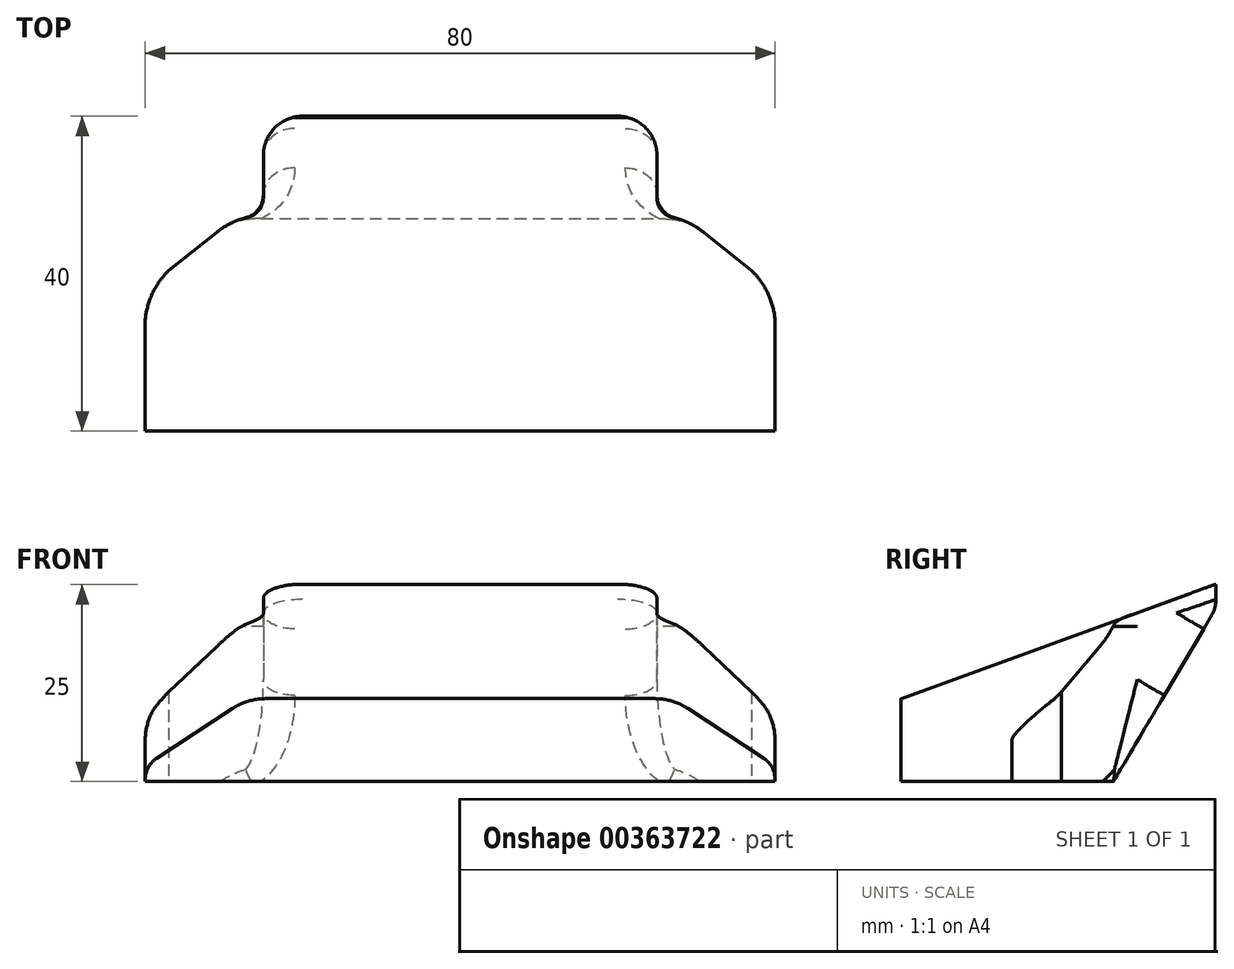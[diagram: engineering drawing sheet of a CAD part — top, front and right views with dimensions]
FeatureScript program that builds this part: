
annotation { "Feature Type Name" : "Feature", "Feature Type Description" : "" }
export const myFeature = defineFeature(function(context is Context, id is Id, definition is map)
    precondition{}
    {
        {
            var Q0;
            Q0=qCreatedBy(makeId("Top.planeOp"),FACE);
            var sketch = newSketch(context, id + "F0", { "sketchPlane" : qUnion([Q0])});
            skLineSegment(sketch, "E0", {"start": v(40, 0) * mm, "end": v(-40, 0) * mm});
            skLineSegment(sketch, "E1", {"start": v(-40, 0) * mm, "end": v(-40, 18) * mm});
            skLineSegment(sketch, "E2", {"start": v(-40, 18) * mm, "end": v(-28.75, 27) * mm});
            skLineSegment(sketch, "E3", {"start": v(-28.75, 27) * mm, "end": v(28.75, 27) * mm});
            skLineSegment(sketch, "E4", {"start": v(28.75, 27) * mm, "end": v(40, 18) * mm});
            skLineSegment(sketch, "E5", {"start": v(0, 40) * mm, "end": v(0, 0) * mm, "construction": true});
            skLineSegment(sketch, "E6", {"start": v(40, 18) * mm, "end": v(40, 0) * mm});
            skLineSegment(sketch, "E7", {"start": v(-25, 27) * mm, "end": v(-25, 40) * mm});
            skLineSegment(sketch, "E8", {"start": v(-25, 40) * mm, "end": v(25, 40) * mm});
            skLineSegment(sketch, "E9", {"start": v(25, 40) * mm, "end": v(25, 27) * mm});
            skSolve(sketch);
        }
        {
            var Q0;
            Q0 = qSketchRegion(id + "F0", true);
            extrude(context, id + "F1", {"entities" : qUnion([Q0]), "depth" : 25 * mm, "offsetDistance" : 25 * mm});
        }
        {
            var Q0;
            Q0=makeQuery(id+"F1.opExtrude","CAP_EDGE",EDGE,{"disambiguationData":[OSD([sQuery(id+"F0.wireOp",EDGE,"E0")])],"isStart":false});
            chamfer(context, id + "F2", {"entities" : qUnion([Q0]), "chamferType" : ChamferType.OFFSET_ANGLE, "width" : 14.5 * mm, "oppositeDirection" : false, "angle" : 70 * degree, "tangentPropagation" : true});
        }
        {
            var Q0;
            Q0=makeQuery(id+"F1.opExtrude","CAP_EDGE",EDGE,{"disambiguationData":[OSD([sQuery(id+"F0.wireOp",EDGE,"E8")])],"isStart":true});
            chamfer(context, id + "F3", {"entities" : qUnion([Q0]), "chamferType" : ChamferType.TWO_OFFSETS, "width1" : 13 * mm, "oppositeDirection" : false, "width2" : 22 * mm, "tangentPropagation" : true});
        }
        {
            var Q0;
            Q0=makeQuery(id+"F2.opChamfer","BLEND_EDGE",EDGE,{"blendedFrom":[makeQuery(id+"F1.opExtrude","CAP_EDGE",EDGE,{"disambiguationData":[OSD([sQuery(id+"F0.wireOp",EDGE,"E0")])],"isStart":false}),makeQuery(id+"F1.opExtrude","SWEPT_FACE",FACE,{"disambiguationData":[OSD([sQuery(id+"F0.wireOp",EDGE,"E1")])]})],"blendedInto":[makeQuery(id+"F1.opExtrude","SWEPT_FACE",FACE,{"disambiguationData":[OSD([sQuery(id+"F0.wireOp",EDGE,"E1")])]})]});
            var Q1;
            Q1=makeQuery(id+"F2.opChamfer","BLEND_EDGE",EDGE,{"blendedFrom":[makeQuery(id+"F1.opExtrude","CAP_EDGE",EDGE,{"disambiguationData":[OSD([sQuery(id+"F0.wireOp",EDGE,"E0")])],"isStart":false}),makeQuery(id+"F1.opExtrude","SWEPT_FACE",FACE,{"disambiguationData":[OSD([sQuery(id+"F0.wireOp",EDGE,"E6")])]})],"blendedInto":[makeQuery(id+"F1.opExtrude","SWEPT_FACE",FACE,{"disambiguationData":[OSD([sQuery(id+"F0.wireOp",EDGE,"E6")])]})]});
            chamfer(context, id + "F4", {"entities" : qUnion([Q0, Q1]), "chamferType" : ChamferType.TWO_OFFSETS, "width1" : 8 * mm, "oppositeDirection" : false, "width2" : 13 * mm, "tangentPropagation" : true});
        }
        {
            var Q0;
            Q0=makeQuery(id+"F1.opExtrude","SWEPT_EDGE",EDGE,{"disambiguationData":[OSD([sQuery(id+"F0.wireOp",EDGE,"E3"),sQuery(id+"F0.wireOp",EDGE,"E9")])]});
            var Q1;
            Q1=makeQuery(id+"F1.opExtrude","SWEPT_EDGE",EDGE,{"disambiguationData":[OSD([sQuery(id+"F0.wireOp",EDGE,"E3"),sQuery(id+"F0.wireOp",EDGE,"E7")])]});
            fillet(context, id + "F5", {"entities" : qUnion([Q0, Q1]), "tangentPropagation" : true, "radius" : 3 * mm, "defaultsChanged" : true, "vertexSettings" : [], "allowEdgeOverflow" : false});
        }
        {
            var Q0;
            Q0=makeQuery(id+"F1.opExtrude","SWEPT_BODY",BODY,{"disambiguationData":[OSD([sQuery(id+"F0.wireOp",EDGE,"E0"),sQuery(id+"F0.wireOp",EDGE,"E1"),sQuery(id+"F0.wireOp",EDGE,"E2"),sQuery(id+"F0.wireOp",EDGE,"E3"),sQuery(id+"F0.wireOp",EDGE,"E4"),sQuery(id+"F0.wireOp",EDGE,"E6"),sQuery(id+"F0.wireOp",EDGE,"E7"),sQuery(id+"F0.wireOp",EDGE,"E8"),sQuery(id+"F0.wireOp",EDGE,"E9")])]});
            var Q1;
            Q1=qCreatedBy(makeId("Origin.pointOp"),VERTEX);
            transform(context, id + "F6", {"entities" : qUnion([Q0]), "transformType" : TransformType.SCALE_UNIFORMLY, "scale" : 1, "scalePoint" : qUnion([Q1]), "makeCopy" : true});
        }
        {
            var Q0;
            Q0=makeQuery(id+"F1.opExtrude","SWEPT_EDGE",EDGE,{"disambiguationData":[OSD([sQuery(id+"F0.wireOp",EDGE,"E2"),sQuery(id+"F0.wireOp",EDGE,"E3")])]});
            var Q1;
            Q1=makeQuery(id+"F1.opExtrude","SWEPT_EDGE",EDGE,{"disambiguationData":[OSD([sQuery(id+"F0.wireOp",EDGE,"E3"),sQuery(id+"F0.wireOp",EDGE,"E4")])]});
            fillet(context, id + "F7", {"entities" : qUnion([Q0, Q1]), "tangentPropagation" : true, "radius" : 10 * mm, "defaultsChanged" : true, "vertexSettings" : [], "allowEdgeOverflow" : false});
        }
        {
            var Q0;
            Q0=makeQuery(id+"F1.opExtrude","SWEPT_EDGE",EDGE,{"disambiguationData":[OSD([sQuery(id+"F0.wireOp",EDGE,"E7"),sQuery(id+"F0.wireOp",EDGE,"E8")])]});
            var Q1;
            Q1=makeQuery(id+"F1.opExtrude","SWEPT_EDGE",EDGE,{"disambiguationData":[OSD([sQuery(id+"F0.wireOp",EDGE,"E8"),sQuery(id+"F0.wireOp",EDGE,"E9")])]});
            fillet(context, id + "F8", {"entities" : qUnion([Q0, Q1]), "tangentPropagation" : true, "radius" : 5 * mm, "defaultsChanged" : true, "vertexSettings" : [], "allowEdgeOverflow" : false});
        }
        {
            var Q0;
            {var subQ0=sQuery(id+"F0.wireOp",EDGE,"E8");Q0=makeQuery(id+"F3.opChamfer","BLEND_EDGE",EDGE,{"blendedFrom":[makeQuery(id+"F1.opExtrude","CAP_EDGE",EDGE,{"disambiguationData":[OSD([subQ0])],"isStart":true}),makeQuery(id+"F1.opExtrude","SWEPT_FACE",FACE,{"disambiguationData":[OSD([subQ0])]})],"blendedInto":[makeQuery(id+"F1.opExtrude","SWEPT_FACE",FACE,{"disambiguationData":[OSD([subQ0])]})]});}
            var Q1;
            {var subQ0=sQuery(id+"F0.wireOp",EDGE,"E8");Q1=makeQuery(id+"F8.opFillet","BLEND_EDGE",EDGE,{"blendedFrom":[makeQuery(id+"F1.opExtrude","SWEPT_EDGE",EDGE,{"disambiguationData":[OSD([sQuery(id+"F0.wireOp",EDGE,"E7"),subQ0])]}),makeQuery(id+"F3.opChamfer","BLEND_FACE",FACE,{"disambiguationData":[OSD([subQ0])]})],"blendedInto":[makeQuery(id+"F3.opChamfer","BLEND_FACE",FACE,{"disambiguationData":[OSD([subQ0])]})]});}
            var Q2;
            Q2=makeQuery(id+"F3.opChamfer","BLEND_EDGE",EDGE,{"blendedFrom":[makeQuery(id+"F1.opExtrude","CAP_EDGE",EDGE,{"disambiguationData":[OSD([sQuery(id+"F0.wireOp",EDGE,"E8")])],"isStart":true}),makeQuery(id+"F1.opExtrude","SWEPT_FACE",FACE,{"disambiguationData":[OSD([sQuery(id+"F0.wireOp",EDGE,"E7")])]})],"blendedInto":[makeQuery(id+"F1.opExtrude","SWEPT_FACE",FACE,{"disambiguationData":[OSD([sQuery(id+"F0.wireOp",EDGE,"E7")])]})]});
            var Q3;
            Q3=makeQuery(id+"F5.opFillet","BLEND_EDGE",EDGE,{"blendedFrom":[makeQuery(id+"F1.opExtrude","SWEPT_EDGE",EDGE,{"disambiguationData":[OSD([sQuery(id+"F0.wireOp",EDGE,"E3"),sQuery(id+"F0.wireOp",EDGE,"E7")])]}),makeQuery(id+"F3.opChamfer","BLEND_FACE",FACE,{"disambiguationData":[OSD([sQuery(id+"F0.wireOp",EDGE,"E8")])]})],"blendedInto":[makeQuery(id+"F3.opChamfer","BLEND_FACE",FACE,{"disambiguationData":[OSD([sQuery(id+"F0.wireOp",EDGE,"E8")])]})]});
            var Q4;
            Q4=makeQuery(id+"F5.opFillet","BLEND_EDGE",EDGE,{"blendedFrom":[makeQuery(id+"F1.opExtrude","SWEPT_EDGE",EDGE,{"disambiguationData":[OSD([sQuery(id+"F0.wireOp",EDGE,"E3"),sQuery(id+"F0.wireOp",EDGE,"E9")])]}),makeQuery(id+"F3.opChamfer","BLEND_FACE",FACE,{"disambiguationData":[OSD([sQuery(id+"F0.wireOp",EDGE,"E8")])]})],"blendedInto":[makeQuery(id+"F3.opChamfer","BLEND_FACE",FACE,{"disambiguationData":[OSD([sQuery(id+"F0.wireOp",EDGE,"E8")])]})]});
            var Q5;
            Q5=makeQuery(id+"F3.opChamfer","BLEND_EDGE",EDGE,{"blendedFrom":[makeQuery(id+"F1.opExtrude","CAP_EDGE",EDGE,{"disambiguationData":[OSD([sQuery(id+"F0.wireOp",EDGE,"E8")])],"isStart":true}),makeQuery(id+"F1.opExtrude","SWEPT_FACE",FACE,{"disambiguationData":[OSD([sQuery(id+"F0.wireOp",EDGE,"E9")])]})],"blendedInto":[makeQuery(id+"F1.opExtrude","SWEPT_FACE",FACE,{"disambiguationData":[OSD([sQuery(id+"F0.wireOp",EDGE,"E9")])]})]});
            var Q6;
            {var subQ0=sQuery(id+"F0.wireOp",EDGE,"E8");Q6=makeQuery(id+"F8.opFillet","BLEND_EDGE",EDGE,{"blendedFrom":[makeQuery(id+"F1.opExtrude","SWEPT_EDGE",EDGE,{"disambiguationData":[OSD([subQ0,sQuery(id+"F0.wireOp",EDGE,"E9")])]}),makeQuery(id+"F3.opChamfer","BLEND_FACE",FACE,{"disambiguationData":[OSD([subQ0])]})],"blendedInto":[makeQuery(id+"F3.opChamfer","BLEND_FACE",FACE,{"disambiguationData":[OSD([subQ0])]})]});}
            fillet(context, id + "F9", {"entities" : qUnion([Q0, Q1, Q2, Q3, Q4, Q5, Q6]), "tangentPropagation" : true, "radius" : 4 * mm, "defaultsChanged" : true, "vertexSettings" : [], "allowEdgeOverflow" : false});
        }
        {
            var Q0;
            {var subQ0=sQuery(id+"F0.wireOp",EDGE,"E0");Q0=makeQuery(id+"F4.opChamfer","BLEND_EDGE",EDGE,{"blendedFrom":[makeQuery(id+"F2.opChamfer","BLEND_EDGE",EDGE,{"blendedFrom":[makeQuery(id+"F1.opExtrude","CAP_EDGE",EDGE,{"disambiguationData":[OSD([subQ0])],"isStart":false}),makeQuery(id+"F1.opExtrude","SWEPT_FACE",FACE,{"disambiguationData":[OSD([sQuery(id+"F0.wireOp",EDGE,"E1")])]})],"blendedInto":[makeQuery(id+"F1.opExtrude","SWEPT_FACE",FACE,{"disambiguationData":[OSD([sQuery(id+"F0.wireOp",EDGE,"E1")])]})]}),makeQuery(id+"F2.opChamfer","BLEND_FACE",FACE,{"disambiguationData":[OSD([subQ0])]})],"blendedInto":[makeQuery(id+"F2.opChamfer","BLEND_FACE",FACE,{"disambiguationData":[OSD([subQ0])]})]});}
            var Q1;
            {var subQ0=sQuery(id+"F0.wireOp",EDGE,"E0");Q1=makeQuery(id+"F4.opChamfer","BLEND_EDGE",EDGE,{"blendedFrom":[makeQuery(id+"F2.opChamfer","BLEND_EDGE",EDGE,{"blendedFrom":[makeQuery(id+"F1.opExtrude","CAP_EDGE",EDGE,{"disambiguationData":[OSD([subQ0])],"isStart":false}),makeQuery(id+"F1.opExtrude","SWEPT_FACE",FACE,{"disambiguationData":[OSD([sQuery(id+"F0.wireOp",EDGE,"E6")])]})],"blendedInto":[makeQuery(id+"F1.opExtrude","SWEPT_FACE",FACE,{"disambiguationData":[OSD([sQuery(id+"F0.wireOp",EDGE,"E6")])]})]}),makeQuery(id+"F2.opChamfer","BLEND_FACE",FACE,{"disambiguationData":[OSD([subQ0])]})],"blendedInto":[makeQuery(id+"F2.opChamfer","BLEND_FACE",FACE,{"disambiguationData":[OSD([subQ0])]})]});}
            fillet(context, id + "F10", {"entities" : qUnion([Q0, Q1]), "tangentPropagation" : true, "radius" : 8 * mm, "defaultsChanged" : true, "vertexSettings" : [], "allowEdgeOverflow" : false});
        }
        {
            var Q0;
            {var subQ0=makeQuery(id+"F1.opExtrude","SWEPT_FACE",FACE,{"disambiguationData":[OSD([sQuery(id+"F0.wireOp",EDGE,"E6")])]});Q0=makeQuery(id+"F4.opChamfer","BLEND_EDGE",EDGE,{"blendedFrom":[makeQuery(id+"F2.opChamfer","BLEND_EDGE",EDGE,{"blendedFrom":[makeQuery(id+"F1.opExtrude","CAP_EDGE",EDGE,{"disambiguationData":[OSD([sQuery(id+"F0.wireOp",EDGE,"E0")])],"isStart":false}),subQ0],"blendedInto":[subQ0]}),subQ0],"blendedInto":[subQ0]});}
            var Q1;
            {var subQ0=makeQuery(id+"F1.opExtrude","SWEPT_FACE",FACE,{"disambiguationData":[OSD([sQuery(id+"F0.wireOp",EDGE,"E1")])]});Q1=makeQuery(id+"F4.opChamfer","BLEND_EDGE",EDGE,{"blendedFrom":[makeQuery(id+"F2.opChamfer","BLEND_EDGE",EDGE,{"blendedFrom":[makeQuery(id+"F1.opExtrude","CAP_EDGE",EDGE,{"disambiguationData":[OSD([sQuery(id+"F0.wireOp",EDGE,"E0")])],"isStart":false}),subQ0],"blendedInto":[subQ0]}),subQ0],"blendedInto":[subQ0]});}
            fillet(context, id + "F11", {"entities" : qUnion([Q0, Q1]), "tangentPropagation" : true, "radius" : 3 * mm, "defaultsChanged" : true, "vertexSettings" : [], "allowEdgeOverflow" : false});
        }
        {
            var Q0;
            Q0=makeQuery(id+"F6.opPattern","COPY",BODY,{"derivedFrom":makeQuery(id+"F1.opExtrude","SWEPT_BODY",BODY,{"disambiguationData":[OSD([sQuery(id+"F0.wireOp",EDGE,"E0"),sQuery(id+"F0.wireOp",EDGE,"E1"),sQuery(id+"F0.wireOp",EDGE,"E2"),sQuery(id+"F0.wireOp",EDGE,"E3"),sQuery(id+"F0.wireOp",EDGE,"E4"),sQuery(id+"F0.wireOp",EDGE,"E6"),sQuery(id+"F0.wireOp",EDGE,"E7"),sQuery(id+"F0.wireOp",EDGE,"E8"),sQuery(id+"F0.wireOp",EDGE,"E9")])]}),"instanceName":"1"});
            var Q1;
            {var subQ0=sQuery(id+"F0.wireOp",EDGE,"E0");var subQ1=makeQuery(id+"F2.opChamfer","BLEND_FACE",FACE,{"disambiguationData":[OSD([subQ0])]});Q1=makeQuery(id+"F6.opPattern","COPY",EDGE,{"derivedFrom":makeQuery(id+"F10.opFillet","BLEND_EDGE",EDGE,{"blendedFrom":[makeQuery(id+"F4.opChamfer","BLEND_EDGE",EDGE,{"blendedFrom":[makeQuery(id+"F2.opChamfer","BLEND_EDGE",EDGE,{"blendedFrom":[makeQuery(id+"F1.opExtrude","CAP_EDGE",EDGE,{"disambiguationData":[OSD([subQ0])],"isStart":false}),makeQuery(id+"F1.opExtrude","SWEPT_FACE",FACE,{"disambiguationData":[OSD([sQuery(id+"F0.wireOp",EDGE,"E1")])]})],"blendedInto":[makeQuery(id+"F1.opExtrude","SWEPT_FACE",FACE,{"disambiguationData":[OSD([sQuery(id+"F0.wireOp",EDGE,"E1")])]})]}),subQ1],"blendedInto":[subQ1]}),subQ1],"blendedInto":[subQ1]}),"instanceName":"1"});}
            transform(context, id + "F12", {"entities" : qUnion([Q0]), "transformType" : TransformType.TRANSLATION_3D, "dx" : 0 * mm, "dy" : 0.01 * mm, "dz" : 0 * mm, "makeCopy" : false});
        }
        {
            var Q0;
            Q0=makeQuery(id+"F6.opPattern","COPY",EDGE,{"derivedFrom":makeQuery(id+"F1.opExtrude","SWEPT_EDGE",EDGE,{"disambiguationData":[OSD([sQuery(id+"F0.wireOp",EDGE,"E1"),sQuery(id+"F0.wireOp",EDGE,"E2")])]}),"instanceName":"1"});
            var Q1;
            Q1=makeQuery(id+"F6.opPattern","COPY",EDGE,{"derivedFrom":makeQuery(id+"F1.opExtrude","SWEPT_EDGE",EDGE,{"disambiguationData":[OSD([sQuery(id+"F0.wireOp",EDGE,"E4"),sQuery(id+"F0.wireOp",EDGE,"E6")])]}),"instanceName":"1"});
            fillet(context, id + "F13", {"entities" : qUnion([Q0, Q1]), "tangentPropagation" : true, "radius" : 10 * mm, "defaultsChanged" : true, "vertexSettings" : [], "allowEdgeOverflow" : false});
        }
        {
            var Q0;
            Q0=makeQuery(id+"F1.opExtrude","SWEPT_BODY",BODY,{"disambiguationData":[OSD([sQuery(id+"F0.wireOp",EDGE,"E0"),sQuery(id+"F0.wireOp",EDGE,"E1"),sQuery(id+"F0.wireOp",EDGE,"E2"),sQuery(id+"F0.wireOp",EDGE,"E3"),sQuery(id+"F0.wireOp",EDGE,"E4"),sQuery(id+"F0.wireOp",EDGE,"E6"),sQuery(id+"F0.wireOp",EDGE,"E7"),sQuery(id+"F0.wireOp",EDGE,"E8"),sQuery(id+"F0.wireOp",EDGE,"E9")])]});
            var Q1;
            Q1=makeQuery(id+"F6.opPattern","COPY",BODY,{"derivedFrom":makeQuery(id+"F1.opExtrude","SWEPT_BODY",BODY,{"disambiguationData":[OSD([sQuery(id+"F0.wireOp",EDGE,"E0"),sQuery(id+"F0.wireOp",EDGE,"E1"),sQuery(id+"F0.wireOp",EDGE,"E2"),sQuery(id+"F0.wireOp",EDGE,"E3"),sQuery(id+"F0.wireOp",EDGE,"E4"),sQuery(id+"F0.wireOp",EDGE,"E6"),sQuery(id+"F0.wireOp",EDGE,"E7"),sQuery(id+"F0.wireOp",EDGE,"E8"),sQuery(id+"F0.wireOp",EDGE,"E9")])]}),"instanceName":"1"});
            booleanBodies(context, id + "F14", {"operationType" : BooleanOperationType.INTERSECTION, "tools" : qUnion([Q0, Q1])});
        }
    });
